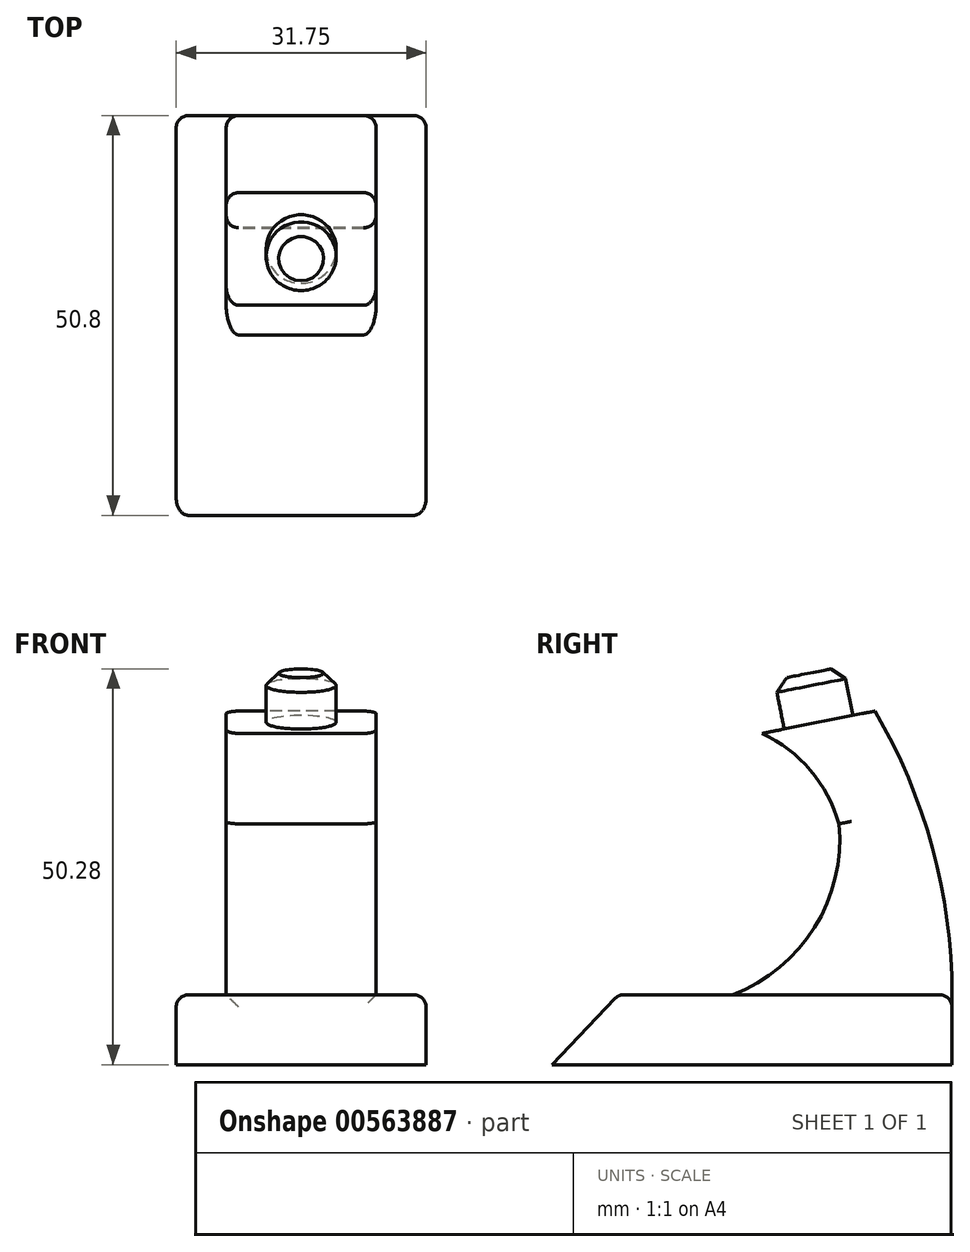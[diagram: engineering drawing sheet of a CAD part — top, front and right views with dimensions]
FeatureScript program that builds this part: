
annotation { "Feature Type Name" : "Feature", "Feature Type Description" : "" }
export const myFeature = defineFeature(function(context is Context, id is Id, definition is map)
    precondition{}
    {
        {
            var Q0;
            Q0=qCreatedBy(makeId("Right.planeOp"),FACE);
            var sketch = newSketch(context, id + "F0", { "sketchPlane" : qUnion([Q0])});
            skLineSegment(sketch, "E0", {"start": v(0, 0) * mm, "end": v(50.8, 0) * mm});
            skLineSegment(sketch, "E1", {"start": v(50.8, 0) * mm, "end": v(50.8, 8.9) * mm});
            skLineSegment(sketch, "E2", {"start": v(22.91, 8.9) * mm, "end": v(8.44, 8.9) * mm});
            skLineSegment(sketch, "E3", {"start": v(8.44, 8.89) * mm, "end": v(0, 0) * mm});
            skArc(sketch, "E4", {"start": v(22.91, 8.9) * mm, "mid": v(33.35, 17.46) * mm, "end": v(36.44, 30.6) * mm});
            skArc(sketch, "E5", {"start": v(36.44, 30.6) * mm, "mid": v(32.8, 37.4) * mm, "end": v(26.69, 42.08) * mm});
            skLineSegment(sketch, "E6", {"start": v(26.69, 42.08) * mm, "end": v(41, 44.91) * mm});
            skArc(sketch, "E7", {"start": v(50.8, 8.9) * mm, "mid": v(48.3, 27.56) * mm, "end": v(41, 44.91) * mm});
            skSolve(sketch);
        }
        {
            var Q0;
            Q0=makeQuery(id+"F0.imprint","IMPRINT",FACE,{"disambiguationData":[TD([[makeQuery(id+"F0.imprint","IMPRINT",EDGE,{"derivedFrom":sQuery(id+"F0.wireOp",EDGE,"E0")}),1.0]])]});
            extrude(context, id + "F1", {"entities" : qUnion([Q0]), "depth" : 19.05 * mm, "offsetDistance" : 25.4 * mm});
        }
        {
            var Q0;
            Q0=makeQuery(id+"F1.opExtrude","CAP_FACE",FACE,{"disambiguationData":[OSD([sQuery(id+"F0.wireOp",EDGE,"E0"),sQuery(id+"F0.wireOp",EDGE,"E1"),sQuery(id+"F0.wireOp",EDGE,"E2"),sQuery(id+"F0.wireOp",EDGE,"E3"),sQuery(id+"F0.wireOp",EDGE,"E4"),sQuery(id+"F0.wireOp",EDGE,"E5"),sQuery(id+"F0.wireOp",EDGE,"E6"),sQuery(id+"F0.wireOp",EDGE,"E7")])],"isStart":false});
            var sketch = newSketch(context, id + "F2", { "sketchPlane" : qUnion([Q0])});
            skLineSegment(sketch, "E8", {"start": v(0, 0) * mm, "end": v(8.44, 8.89) * mm});
            skLineSegment(sketch, "E9", {"start": v(8.44, 8.89) * mm, "end": v(50.8, 8.89) * mm});
            skLineSegment(sketch, "E10", {"start": v(50.8, 8.89) * mm, "end": v(50.8, 0) * mm});
            skLineSegment(sketch, "E11", {"start": v(50.8, 0) * mm, "end": v(0, 0) * mm});
            skSolve(sketch);
        }
        {
            var Q0;
            {var subQ3=sQuery(id+"F2.wireOp",EDGE,"E8");Q0=makeQuery(id+"F2.imprint","IMPRINT",FACE,{"disambiguationData":[TD([[makeQuery(id+"F2.imprint","IMPRINT",EDGE,{"derivedFrom":subQ3}),1.0]])]});}
            extrude(context, id + "F3", {"entities" : qUnion([Q0]), "operationType" : NewBodyOperationType.ADD, "depth" : 6.35 * mm, "offsetDistance" : 25.4 * mm});
        }
        {
            var Q0;
            Q0=makeQuery(id+"F1.opExtrude","CAP_FACE",FACE,{"disambiguationData":[OSD([sQuery(id+"F0.wireOp",EDGE,"E0"),sQuery(id+"F0.wireOp",EDGE,"E1"),sQuery(id+"F0.wireOp",EDGE,"E2"),sQuery(id+"F0.wireOp",EDGE,"E3"),sQuery(id+"F0.wireOp",EDGE,"E4"),sQuery(id+"F0.wireOp",EDGE,"E5"),sQuery(id+"F0.wireOp",EDGE,"E6"),sQuery(id+"F0.wireOp",EDGE,"E7")])],"isStart":true});
            var sketch = newSketch(context, id + "F4", { "sketchPlane" : qUnion([Q0])});
            skLineSegment(sketch, "E12", {"start": v(0, 0) * mm, "end": v(-8.44, 8.89) * mm});
            skLineSegment(sketch, "E13", {"start": v(-8.44, 8.89) * mm, "end": v(-50.8, 8.89) * mm});
            skLineSegment(sketch, "E14", {"start": v(-50.8, 8.89) * mm, "end": v(-50.8, 0) * mm});
            skLineSegment(sketch, "E15", {"start": v(-50.8, 0) * mm, "end": v(0, 0) * mm});
            skSolve(sketch);
        }
        {
            var Q0;
            {var subQ3=sQuery(id+"F4.wireOp",EDGE,"E12");Q0=makeQuery(id+"F4.imprint","IMPRINT",FACE,{"disambiguationData":[TD([[makeQuery(id+"F4.imprint","IMPRINT",EDGE,{"derivedFrom":subQ3}),-1.0]])]});}
            extrude(context, id + "F5", {"entities" : qUnion([Q0]), "operationType" : NewBodyOperationType.ADD, "depth" : 6.35 * mm, "offsetDistance" : 25.4 * mm});
        }
        {
            var Q0;
            Q0=makeQuery(id+"F1.opExtrude","SWEPT_FACE",FACE,{"disambiguationData":[OSD([sQuery(id+"F0.wireOp",EDGE,"E6")])]});
            var sketch = newSketch(context, id + "F6", { "sketchPlane" : qUnion([Q0])});
            skLineSegment(sketch, "E16", {"start": v(0, 48.93) * mm, "end": v(19.05, 34.34) * mm, "construction": true});
            skLineSegment(sketch, "E17", {"start": v(0, 34.34) * mm, "end": v(19.05, 48.93) * mm, "construction": true});
            skCircle(sketch, "E18", {"center": v(9.53, 41.64) * mm, "radius": 4.45 * mm});
            skSolve(sketch);
        }
        {
            var Q0;
            Q0=makeQuery(id+"F6.imprint","IMPRINT",FACE,{"disambiguationData":[TD([[makeQuery(id+"F6.imprint","IMPRINT",EDGE,{"derivedFrom":sQuery(id+"F6.wireOp",EDGE,"E18")}),1.0]])]});
            extrude(context, id + "F7", {"entities" : qUnion([Q0]), "operationType" : NewBodyOperationType.ADD, "depth" : 6.35 * mm, "offsetDistance" : 25.4 * mm});
        }
        {
            var Q0;
            Q0=makeQuery(id+"F7.opExtrude","CAP_EDGE",EDGE,{"disambiguationData":[OSD([sQuery(id+"F6.wireOp",EDGE,"E18")])],"isStart":false});
            chamfer(context, id + "F8", {"entities" : qUnion([Q0]), "width" : 1.59 * mm, "tangentPropagation" : true});
        }
        {
            var Q0;
            Q0=makeQuery(id+"F1.opExtrude","CAP_EDGE",EDGE,{"disambiguationData":[OSD([sQuery(id+"F0.wireOp",EDGE,"E4")])],"isStart":false});
            var Q1;
            Q1=makeQuery(id+"F1.opExtrude","CAP_EDGE",EDGE,{"disambiguationData":[OSD([sQuery(id+"F0.wireOp",EDGE,"E5")])],"isStart":false});
            var Q2;
            Q2=makeQuery(id+"F1.opExtrude","CAP_EDGE",EDGE,{"disambiguationData":[OSD([sQuery(id+"F0.wireOp",EDGE,"E4")])],"isStart":true});
            var Q3;
            Q3=makeQuery(id+"F1.opExtrude","CAP_EDGE",EDGE,{"disambiguationData":[OSD([sQuery(id+"F0.wireOp",EDGE,"E5")])],"isStart":true});
            var Q4;
            Q4=makeQuery(id+"F1.opExtrude","CAP_EDGE",EDGE,{"disambiguationData":[OSD([sQuery(id+"F0.wireOp",EDGE,"E7")])],"isStart":false});
            var Q5;
            Q5=makeQuery(id+"F1.opExtrude","CAP_EDGE",EDGE,{"disambiguationData":[OSD([sQuery(id+"F0.wireOp",EDGE,"E7")])],"isStart":true});
            var Q6;
            Q6=makeQuery(id+"F3.opExtrude","CAP_EDGE",EDGE,{"disambiguationData":[OSD([sQuery(id+"F2.wireOp",EDGE,"E9")])],"isStart":false});
            var Q7;
            Q7=makeQuery(id+"F5.opExtrude","CAP_EDGE",EDGE,{"disambiguationData":[OSD([sQuery(id+"F4.wireOp",EDGE,"E13")])],"isStart":false});
            var Q8;
            Q8=makeQuery(id+"F5.opExtrude","CAP_EDGE",EDGE,{"disambiguationData":[OSD([sQuery(id+"F4.wireOp",EDGE,"E12")])],"isStart":false});
            var Q9;
            Q9=makeQuery(id+"F3.opExtrude","CAP_EDGE",EDGE,{"disambiguationData":[OSD([sQuery(id+"F2.wireOp",EDGE,"E8")])],"isStart":false});
            var Q10;
            Q10=makeQuery(id+"F3.opExtrude","CAP_EDGE",EDGE,{"disambiguationData":[OSD([sQuery(id+"F2.wireOp",EDGE,"E10")])],"isStart":false});
            var Q11;
            Q11=makeQuery(id+"F3.opExtrude","SWEPT_EDGE",EDGE,{"disambiguationData":[OSD([sQuery(id+"F0.wireOp",EDGE,"E7"),sQuery(id+"F2.wireOp",EDGE,"E9"),sQuery(id+"F2.wireOp",EDGE,"E10")])]});
            var Q12;
            Q12=makeQuery(id+"F5.opExtrude","SWEPT_EDGE",EDGE,{"disambiguationData":[OSD([sQuery(id+"F0.wireOp",EDGE,"E7"),sQuery(id+"F4.wireOp",EDGE,"E13"),sQuery(id+"F4.wireOp",EDGE,"E14")])]});
            var Q13;
            Q13=makeQuery(id+"F5.opExtrude","CAP_EDGE",EDGE,{"disambiguationData":[OSD([sQuery(id+"F4.wireOp",EDGE,"E14")])],"isStart":false});
            var Q14;
            Q14=makeQuery(id+"F5.boolean.opBoolean","MERGE",EDGE,{"derivedFrom":[makeQuery(id+"F3.boolean.opBoolean","MERGE",EDGE,{"derivedFrom":[makeQuery(id+"F1.opExtrude","SWEPT_EDGE",EDGE,{"disambiguationData":[OSD([sQuery(id+"F0.wireOp",EDGE,"E2"),sQuery(id+"F0.wireOp",EDGE,"E3")])]}),makeQuery(id+"F3.opExtrude","SWEPT_EDGE",EDGE,{"disambiguationData":[OSD([sQuery(id+"F2.wireOp",EDGE,"E8"),sQuery(id+"F2.wireOp",EDGE,"E9")])]})]}),makeQuery(id+"F5.opExtrude","SWEPT_EDGE",EDGE,{"disambiguationData":[OSD([sQuery(id+"F4.wireOp",EDGE,"E12"),sQuery(id+"F4.wireOp",EDGE,"E13")])]})]});
            fillet(context, id + "F9", {"entities" : qUnion([Q0, Q1, Q2, Q3, Q4, Q5, Q6, Q7, Q8, Q9, Q10, Q11, Q12, Q13, Q14]), "radius" : 1.59 * mm, "tangentPropagation" : true, "allowEdgeOverflow" : false});
        }
    });
